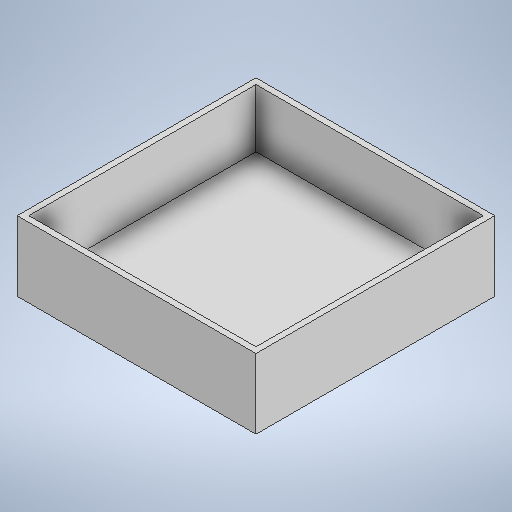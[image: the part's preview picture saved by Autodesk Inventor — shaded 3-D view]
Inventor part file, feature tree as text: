
AUTODESK INVENTOR PART (.ipt)
format: ipt  version: 2025.1 (Build 291241000, 241)  size: 233,984 bytes
history: native  units: mm
features: extrude x2, sketch x2, other x1
ambient origin geometry x8: Origin, YZ Plane, XZ Plane, XY Plane, X Axis, Y Axis, Z Axis, Center Point
bodies: Body1 (feature_tree)
feature tree (5):
  other  "Sólido1"
  extrude  "Extrusão1"  Depth=205.0mm
  extrude  "Extrusão2"  Depth=50.0mm
  sketch  "Esboço1"  dims[d0=205.0mm d1=205.0mm]
  sketch  "Esboço2"  dims[d2=100.0mm d3=100.0mm d4=5.0mm d5=5.0mm d6=5.0mm d7=5.0mm d8=60.0mm d9=0.0mm d10=5.0mm d11=5.0mm d12=5.0mm d13=5.0mm d14=50.0mm d15=0.0mm]
